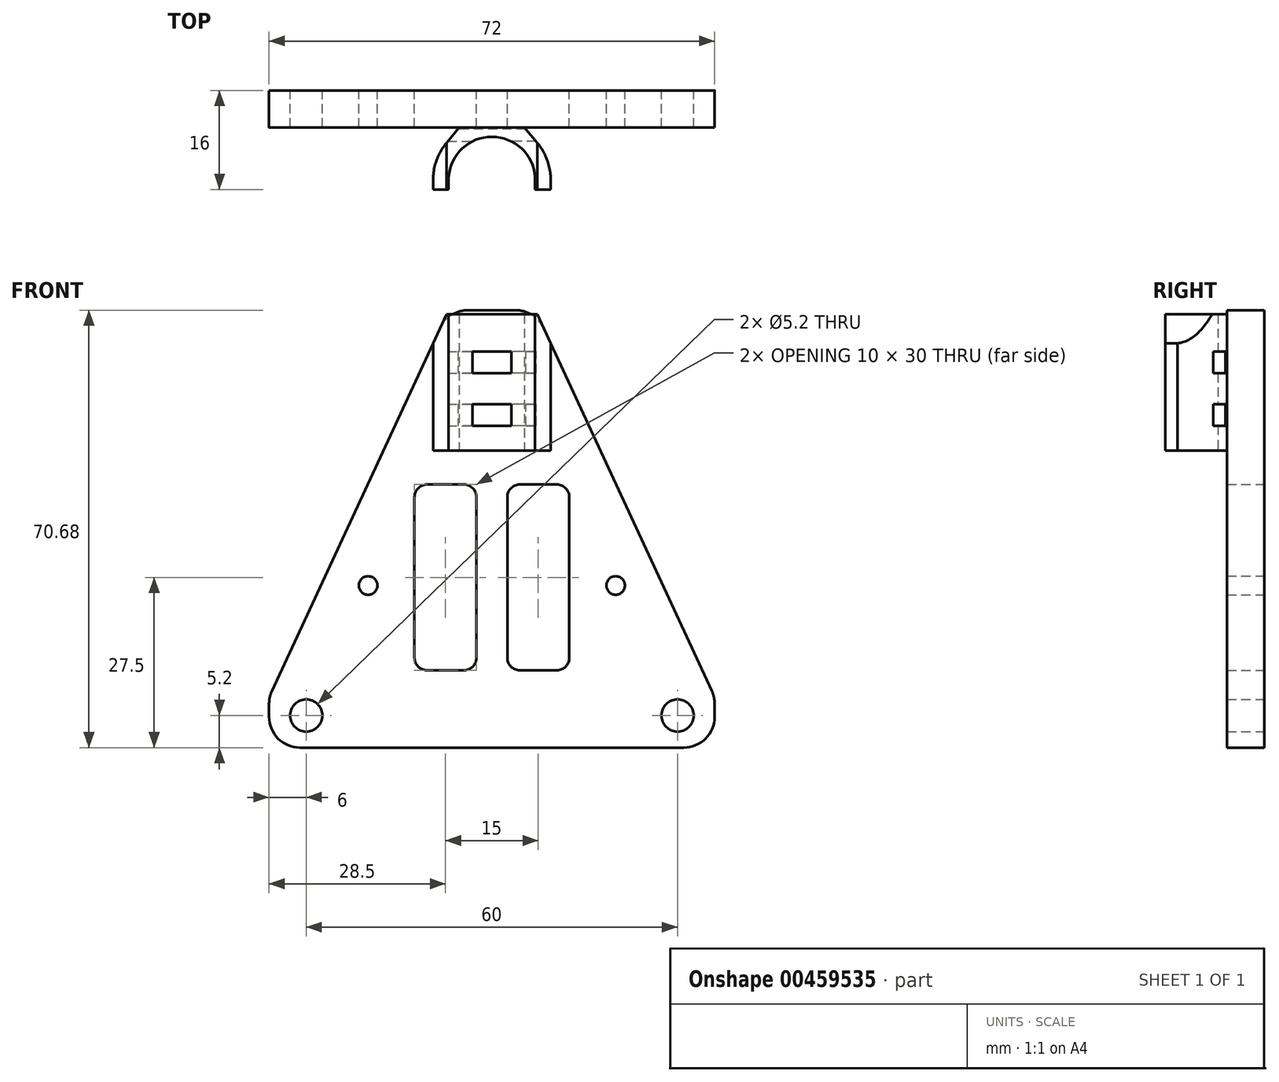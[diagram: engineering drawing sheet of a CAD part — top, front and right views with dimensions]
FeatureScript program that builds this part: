
annotation { "Feature Type Name" : "Feature", "Feature Type Description" : "" }
export const myFeature = defineFeature(function(context is Context, id is Id, definition is map)
    precondition{}
    {
        {
            var Q0;
            Q0=qCreatedBy(makeId("Front.planeOp"),FACE);
            var sketch = newSketch(context, id + "F0", { "sketchPlane" : qUnion([Q0])});
            skCircle(sketch, "E0", {"center": v(-30, 0) * mm, "radius": 2.6 * mm});
            skCircle(sketch, "E1", {"center": v(30, 0) * mm, "radius": 2.6 * mm});
            skLineSegment(sketch, "E2.bottom", {"start": v(-36, -5.2) * mm, "end": v(36, -5.2) * mm});
            skLineSegment(sketch, "E2.top", {"start": v(-36, 65.48) * mm, "end": v(36, 65.48) * mm});
            skLineSegment(sketch, "E2.left", {"start": v(-36, -5.2) * mm, "end": v(-36, 65.48) * mm});
            skLineSegment(sketch, "E2.right", {"start": v(36, -5.2) * mm, "end": v(36, 65.48) * mm});
            skLineSegment(sketch, "E3.bottom", {"start": v(-36, -5.2) * mm, "end": v(36, -5.2) * mm, "construction": true});
            skLineSegment(sketch, "E3.top", {"start": v(-36, 3) * mm, "end": v(36, 3) * mm, "construction": true});
            skLineSegment(sketch, "E3.left", {"start": v(-36, -5.2) * mm, "end": v(-36, 3) * mm, "construction": true});
            skLineSegment(sketch, "E3.right", {"start": v(36, -5.2) * mm, "end": v(36, 3) * mm, "construction": true});
            skLineSegment(sketch, "E4", {"start": v(-36, 3) * mm, "end": v(-5, 69.8) * mm});
            skLineSegment(sketch, "E5", {"start": v(36, 3) * mm, "end": v(5, 69.8) * mm});
            skLineSegment(sketch, "E6", {"start": v(5, 69.8) * mm, "end": v(-5, 69.8) * mm});
            skLineSegment(sketch, "E7.bottom", {"start": v(-12.5, 37.3) * mm, "end": v(-2.5, 37.3) * mm});
            skLineSegment(sketch, "E7.top", {"start": v(-12.5, 7.3) * mm, "end": v(-2.5, 7.3) * mm});
            skLineSegment(sketch, "E7.left", {"start": v(-12.5, 37.3) * mm, "end": v(-12.5, 7.3) * mm});
            skLineSegment(sketch, "E7.right", {"start": v(-2.5, 37.3) * mm, "end": v(-2.5, 7.3) * mm});
            skLineSegment(sketch, "E8.bottom", {"start": v(2.5, 37.3) * mm, "end": v(12.5, 37.3) * mm});
            skLineSegment(sketch, "E8.top", {"start": v(2.5, 7.3) * mm, "end": v(12.5, 7.3) * mm});
            skLineSegment(sketch, "E8.left", {"start": v(2.5, 37.3) * mm, "end": v(2.5, 7.3) * mm});
            skLineSegment(sketch, "E8.right", {"start": v(12.5, 37.3) * mm, "end": v(12.5, 7.3) * mm});
            skCircle(sketch, "E9", {"center": v(-20, 21) * mm, "radius": 1.5 * mm});
            skCircle(sketch, "E10", {"center": v(20, 21) * mm, "radius": 1.5 * mm});
            skSolve(sketch);
        }
        {
            var Q0;
            Q0=makeQuery(id+"F0.imprint","IMPRINT",FACE,{"disambiguationData":[TD([[makeQuery(id+"F0.imprint","IMPRINT",EDGE,{"derivedFrom":sQuery(id+"F0.wireOp",EDGE,"E0")}),-1.0]])]});
            extrude(context, id + "F1", {"entities" : qUnion([Q0]), "depth" : 6 * mm});
        }
        {
            var Q0;
            Q0=makeQuery(id+"F1.opExtrude","CAP_FACE",FACE,{"disambiguationData":[OSD([sQuery(id+"F0.wireOp",EDGE,"E0"),sQuery(id+"F0.wireOp",EDGE,"E1"),sQuery(id+"F0.wireOp",EDGE,"E2.bottom"),sQuery(id+"F0.wireOp",EDGE,"E2.top"),sQuery(id+"F0.wireOp",EDGE,"E2.left"),sQuery(id+"F0.wireOp",EDGE,"E2.right"),sQuery(id+"F0.wireOp",EDGE,"E4"),sQuery(id+"F0.wireOp",EDGE,"E5"),sQuery(id+"F0.wireOp",EDGE,"IImjeFes-nADZ-uSL3-nvNK-4zdbtvGVff6f"),sQuery(id+"F0.wireOp",EDGE,"sDR05uGn-SlpC-Wm0R-yilg-abFSDviSMYJG"),sQuery(id+"F0.wireOp",EDGE,"sjxaUOTC-dEMi-kEfi-0SqV-ZGTUvvVfsrZj"),sQuery(id+"F0.wireOp",EDGE,"LS0tKh8h-u9XM-H1ll-KqjH-JoQgyvfXeunZ")])],"isStart":false});
            var sketch = newSketch(context, id + "F2", { "sketchPlane" : qUnion([Q0])});
            skLineSegment(sketch, "E11.bottom", {"start": v(-10, 64.8) * mm, "end": v(10, 64.8) * mm});
            skLineSegment(sketch, "E11.top", {"start": v(-10, 42.8) * mm, "end": v(10, 42.8) * mm});
            skLineSegment(sketch, "E11.left", {"start": v(-10, 64.8) * mm, "end": v(-10, 42.8) * mm});
            skLineSegment(sketch, "E11.right", {"start": v(10, 64.8) * mm, "end": v(10, 42.8) * mm});
            skSolve(sketch);
        }
        {
            var Q0;
            {var subQ1=sQuery(id+"F2.wireOp",EDGE,"E11.top");Q0=makeQuery(id+"F2.imprint","IMPRINT",FACE,{"disambiguationData":[TD([[makeQuery(id+"F2.imprint","IMPRINT",EDGE,{"derivedFrom":subQ1}),1.0]])]});}
            extrude(context, id + "F3", {"entities" : qUnion([Q0]), "operationType" : NewBodyOperationType.ADD, "depth" : 8 * mm});
        }
        {
            var Q0;
            Q0=makeQuery(id+"F3.opExtrude","SWEPT_FACE",FACE,{"disambiguationData":[OSD([sQuery(id+"F2.wireOp",EDGE,"E11.top")])]});
            var sketch = newSketch(context, id + "F4", { "sketchPlane" : qUnion([Q0])});
            skCircle(sketch, "E12", {"center": v(0, 14.5) * mm, "radius": 7 * mm});
            skPoint(sketch, "E12.centerSnap0", {"position": v(0, 6) * mm});
            skCircle(sketch, "E13", {"center": v(0, 14.5) * mm, "radius": 9.5 * mm});
            skLineSegment(sketch, "E14", {"start": v(3.5, 3.89) * mm, "end": v(7.28, 8.4) * mm});
            skLineSegment(sketch, "E15", {"start": v(-3.5, 3.9) * mm, "end": v(-7.27, 8.4) * mm});
            skSolve(sketch);
        }
        {
            var Q0;
            {var subQ0=sQuery(id+"F4.wireOp",EDGE,"E12");var subQ1=makeQuery(id+"F3.opExtrude","CAP_EDGE",EDGE,{"disambiguationData":[OSD([sQuery(id+"F6hy1r7xXSjZawP_1.wireOp",EDGE,"ysBCCqsK-66z4-jQDk-QU8H-0Tmh3f9Fqvu1.top")])],"isStart":false});var subQ2=makeQuery(id+"F4.imprint","INTERSECT",VERTEX,{"disambiguationData":[OD(0.0)],"derivedFrom":[subQ1,subQ0]});Q0=makeQuery(id+"F4.imprint","IMPRINT",FACE,{"disambiguationData":[TD([[makeQuery(id+"F4.imprint","IMPRINT",EDGE,{"disambiguationData":[TD([[subQ2,-1.0]])],"derivedFrom":subQ0}),1.0]])]});}
            var Q1;
            {var subQ0=sQuery(id+"F4.wireOp",EDGE,"E14");Q1=makeQuery(id+"F4.imprint","IMPRINT",FACE,{"disambiguationData":[TD([[makeQuery(id+"F4.imprint","IMPRINT",EDGE,{"derivedFrom":subQ0}),-1.0]])]});}
            var Q2;
            {var subQ0=sQuery(id+"F4.wireOp",EDGE,"E15");Q2=makeQuery(id+"F4.imprint","IMPRINT",FACE,{"disambiguationData":[TD([[makeQuery(id+"F4.imprint","IMPRINT",EDGE,{"derivedFrom":subQ0}),1.0]])]});}
            extrude(context, id + "F5", {"entities" : qUnion([Q0, Q1, Q2]), "operationType" : NewBodyOperationType.REMOVE, "oppositeDirection" : true, "depth" : 25 * mm});
        }
        {
            var Q0;
            Q0=qCreatedBy(makeId("Right.planeOp"),FACE);
            var sketch = newSketch(context, id + "F6", { "sketchPlane" : qUnion([Q0])});
            skLineSegment(sketch, "E16.bottom", {"start": v(-8.25, 50.3) * mm, "end": v(-6.25, 50.3) * mm});
            skLineSegment(sketch, "E16.top", {"start": v(-8.25, 46.8) * mm, "end": v(-6.25, 46.8) * mm});
            skLineSegment(sketch, "E16.left", {"start": v(-8.25, 50.3) * mm, "end": v(-8.25, 46.8) * mm});
            skLineSegment(sketch, "E16.right", {"start": v(-6.25, 50.3) * mm, "end": v(-6.25, 46.8) * mm});
            skLineSegment(sketch, "E17.bottom", {"start": v(-8.25, 58.8) * mm, "end": v(-6.25, 58.8) * mm});
            skLineSegment(sketch, "E17.top", {"start": v(-8.25, 55.3) * mm, "end": v(-6.25, 55.3) * mm});
            skLineSegment(sketch, "E17.left", {"start": v(-8.25, 58.8) * mm, "end": v(-8.25, 55.3) * mm});
            skLineSegment(sketch, "E17.right", {"start": v(-6.25, 58.8) * mm, "end": v(-6.25, 55.3) * mm});
            skSolve(sketch);
        }
        {
            var Q0;
            Q0 = qSketchRegion(id + "F6", true);
            extrude(context, id + "F7", {"entities" : qUnion([Q0]), "operationType" : NewBodyOperationType.REMOVE, "endBound" : BoundingType.THROUGH_ALL, "depth" : 25 * mm});
        }
        {
            var Q0;
            Q0 = qSketchRegion(id + "F6", true);
            extrude(context, id + "F8", {"entities" : qUnion([Q0]), "operationType" : NewBodyOperationType.REMOVE, "oppositeDirection" : true, "depth" : 25 * mm});
        }
        {
            var Q0;
            Q0=makeQuery(id+"F1.opExtrude","SWEPT_EDGE",EDGE,{"disambiguationData":[OSD([sQuery(id+"F0.wireOp",EDGE,"E2.bottom"),sQuery(id+"F0.wireOp",EDGE,"E2.left")])]});
            var Q1;
            Q1=makeQuery(id+"F1.opExtrude","SWEPT_EDGE",EDGE,{"disambiguationData":[OSD([sQuery(id+"F0.wireOp",EDGE,"E2.bottom"),sQuery(id+"F0.wireOp",EDGE,"E2.right")])]});
            var Q2;
            Q2=makeQuery(id+"F1.opExtrude","SWEPT_EDGE",EDGE,{"disambiguationData":[OSD([sQuery(id+"F0.wireOp",EDGE,"E5"),sQuery(id+"F0.wireOp",EDGE,"E6")])]});
            var Q3;
            Q3=makeQuery(id+"F1.opExtrude","SWEPT_EDGE",EDGE,{"disambiguationData":[OSD([sQuery(id+"F0.wireOp",EDGE,"E4"),sQuery(id+"F0.wireOp",EDGE,"E6")])]});
            var Q4;
            Q4=makeQuery(id+"F1.opExtrude","SWEPT_EDGE",EDGE,{"disambiguationData":[OSD([sQuery(id+"F0.wireOp",EDGE,"E2.right"),sQuery(id+"F0.wireOp",EDGE,"E5")])]});
            var Q5;
            Q5=makeQuery(id+"F1.opExtrude","SWEPT_EDGE",EDGE,{"disambiguationData":[OSD([sQuery(id+"F0.wireOp",EDGE,"E2.left"),sQuery(id+"F0.wireOp",EDGE,"E4")])]});
            var Q6;
            Q6=makeQuery(id+"F1.opExtrude","SWEPT_EDGE",EDGE,{"disambiguationData":[OSD([sQuery(id+"F0.wireOp",EDGE,"IImjeFes-nADZ-uSL3-nvNK-4zdbtvGVff6f"),sQuery(id+"F0.wireOp",EDGE,"sDR05uGn-SlpC-Wm0R-yilg-abFSDviSMYJG")])]});
            var Q7;
            Q7=makeQuery(id+"F1.opExtrude","SWEPT_EDGE",EDGE,{"disambiguationData":[OSD([sQuery(id+"F0.wireOp",EDGE,"IImjeFes-nADZ-uSL3-nvNK-4zdbtvGVff6f"),sQuery(id+"F0.wireOp",EDGE,"LS0tKh8h-u9XM-H1ll-KqjH-JoQgyvfXeunZ")])]});
            var Q8;
            Q8=makeQuery(id+"F1.opExtrude","SWEPT_EDGE",EDGE,{"disambiguationData":[OSD([sQuery(id+"F0.wireOp",EDGE,"sjxaUOTC-dEMi-kEfi-0SqV-ZGTUvvVfsrZj"),sQuery(id+"F0.wireOp",EDGE,"LS0tKh8h-u9XM-H1ll-KqjH-JoQgyvfXeunZ")])]});
            var Q9;
            Q9=makeQuery(id+"F1.opExtrude","SWEPT_EDGE",EDGE,{"disambiguationData":[OSD([sQuery(id+"F0.wireOp",EDGE,"sDR05uGn-SlpC-Wm0R-yilg-abFSDviSMYJG"),sQuery(id+"F0.wireOp",EDGE,"sjxaUOTC-dEMi-kEfi-0SqV-ZGTUvvVfsrZj")])]});
            fillet(context, id + "F9", {"entities" : qUnion([Q0, Q1, Q2, Q3, Q4, Q5, Q6, Q7, Q8, Q9]), "radius" : 5 * mm, "tangentPropagation" : true, "allowEdgeOverflow" : false});
        }
        {
            var Q0;
            {var subQ0=sQuery(id+"F4.wireOp",EDGE,"E13");Q0=makeQuery(id+"F7.boolean.opBoolean","INTERSECT",EDGE,{"derivedFrom":[makeQuery(id+"F5.boolean.opBoolean","COPY",FACE,{"derivedFrom":makeQuery(id+"F5.opExtrude","SWEPT_FACE",FACE,{"disambiguationData":[OSD([subQ0]),TDD([makeQuery(id+"F4.imprint","IMPRINT",EDGE,{"disambiguationData":[TD([[makeQuery(id+"F4.imprint","INTERSECT",VERTEX,{"derivedFrom":[subQ0,sQuery(id+"F4.wireOp",EDGE,"E14")]}),-1.0]])],"derivedFrom":subQ0})])]})}),makeQuery(id+"F7.opExtrude","SWEPT_FACE",FACE,{"disambiguationData":[OSD([sQuery(id+"F6.wireOp",EDGE,"E16.left")])]})]});}
            var Q1;
            {var subQ0=sQuery(id+"F4.wireOp",EDGE,"E13");Q1=makeQuery(id+"F7.boolean.opBoolean","INTERSECT",EDGE,{"derivedFrom":[makeQuery(id+"F5.boolean.opBoolean","COPY",FACE,{"derivedFrom":makeQuery(id+"F5.opExtrude","SWEPT_FACE",FACE,{"disambiguationData":[OSD([subQ0]),TDD([makeQuery(id+"F4.imprint","IMPRINT",EDGE,{"disambiguationData":[TD([[makeQuery(id+"F4.imprint","INTERSECT",VERTEX,{"derivedFrom":[subQ0,sQuery(id+"F4.wireOp",EDGE,"E14")]}),-1.0]])],"derivedFrom":subQ0})])]})}),makeQuery(id+"F7.opExtrude","SWEPT_FACE",FACE,{"disambiguationData":[OSD([sQuery(id+"F6.wireOp",EDGE,"E17.left")])]})]});}
            var Q2;
            {var subQ0=sQuery(id+"F4.wireOp",EDGE,"E13");Q2=makeQuery(id+"F8.boolean.opBoolean","INTERSECT",EDGE,{"derivedFrom":[makeQuery(id+"F5.boolean.opBoolean","COPY",FACE,{"derivedFrom":makeQuery(id+"F5.opExtrude","SWEPT_FACE",FACE,{"disambiguationData":[OSD([subQ0]),TDD([makeQuery(id+"F4.imprint","IMPRINT",EDGE,{"disambiguationData":[TD([[makeQuery(id+"F4.imprint","INTERSECT",VERTEX,{"derivedFrom":[subQ0,sQuery(id+"F4.wireOp",EDGE,"E15")]}),1.0]])],"derivedFrom":subQ0})])]})}),makeQuery(id+"F8.opExtrude","SWEPT_FACE",FACE,{"disambiguationData":[OSD([sQuery(id+"F6.wireOp",EDGE,"E17.left")])]})]});}
            var Q3;
            {var subQ0=sQuery(id+"F4.wireOp",EDGE,"E13");Q3=makeQuery(id+"F8.boolean.opBoolean","INTERSECT",EDGE,{"derivedFrom":[makeQuery(id+"F5.boolean.opBoolean","COPY",FACE,{"derivedFrom":makeQuery(id+"F5.opExtrude","SWEPT_FACE",FACE,{"disambiguationData":[OSD([subQ0]),TDD([makeQuery(id+"F4.imprint","IMPRINT",EDGE,{"disambiguationData":[TD([[makeQuery(id+"F4.imprint","INTERSECT",VERTEX,{"derivedFrom":[subQ0,sQuery(id+"F4.wireOp",EDGE,"E15")]}),1.0]])],"derivedFrom":subQ0})])]})}),makeQuery(id+"F8.opExtrude","SWEPT_FACE",FACE,{"disambiguationData":[OSD([sQuery(id+"F6.wireOp",EDGE,"E16.left")])]})]});}
            var Q4;
            Q4=makeQuery(id+"F1.opExtrude","SWEPT_EDGE",EDGE,{"disambiguationData":[OSD([sQuery(id+"F0.wireOp",EDGE,"E7.bottom"),sQuery(id+"F0.wireOp",EDGE,"E7.left")])]});
            var Q5;
            Q5=makeQuery(id+"F1.opExtrude","SWEPT_EDGE",EDGE,{"disambiguationData":[OSD([sQuery(id+"F0.wireOp",EDGE,"E7.top"),sQuery(id+"F0.wireOp",EDGE,"E7.left")])]});
            var Q6;
            Q6=makeQuery(id+"F1.opExtrude","SWEPT_EDGE",EDGE,{"disambiguationData":[OSD([sQuery(id+"F0.wireOp",EDGE,"E7.top"),sQuery(id+"F0.wireOp",EDGE,"E7.right")])]});
            var Q7;
            Q7=makeQuery(id+"F1.opExtrude","SWEPT_EDGE",EDGE,{"disambiguationData":[OSD([sQuery(id+"F0.wireOp",EDGE,"E8.top"),sQuery(id+"F0.wireOp",EDGE,"E8.right")])]});
            var Q8;
            Q8=makeQuery(id+"F1.opExtrude","SWEPT_EDGE",EDGE,{"disambiguationData":[OSD([sQuery(id+"F0.wireOp",EDGE,"E8.bottom"),sQuery(id+"F0.wireOp",EDGE,"E8.right")])]});
            var Q9;
            Q9=makeQuery(id+"F1.opExtrude","SWEPT_EDGE",EDGE,{"disambiguationData":[OSD([sQuery(id+"F0.wireOp",EDGE,"E7.bottom"),sQuery(id+"F0.wireOp",EDGE,"E7.right")])]});
            var Q10;
            Q10=makeQuery(id+"F1.opExtrude","SWEPT_EDGE",EDGE,{"disambiguationData":[OSD([sQuery(id+"F0.wireOp",EDGE,"E8.bottom"),sQuery(id+"F0.wireOp",EDGE,"E8.left")])]});
            var Q11;
            Q11=makeQuery(id+"F1.opExtrude","SWEPT_EDGE",EDGE,{"disambiguationData":[OSD([sQuery(id+"F0.wireOp",EDGE,"E8.top"),sQuery(id+"F0.wireOp",EDGE,"E8.left")])]});
            fillet(context, id + "F10", {"entities" : qUnion([Q0, Q1, Q2, Q3, Q4, Q5, Q6, Q7, Q8, Q9, Q10, Q11]), "radius" : 2 * mm, "tangentPropagation" : true, "allowEdgeOverflow" : false});
        }
        {
            var Q0;
            {var subQ0=sQuery(id+"F0.wireOp",EDGE,"E4");var subQ1=sQuery(id+"F2.wireOp",EDGE,"E11.top");Q0=makeQuery(id+"F5.boolean.opBoolean","SPLIT",FACE,{"disambiguationData":[TD([makeQuery(id+"F1.opExtrude","SWEPT_FACE",FACE,{"disambiguationData":[OSD([subQ0])]})])],"derivedFrom":makeQuery(id+"F3.opExtrude","CAP_FACE",FACE,{"disambiguationData":[OSD([subQ0,sQuery(id+"F0.wireOp",EDGE,"E5"),sQuery(id+"F2.wireOp",EDGE,"E11.bottom"),subQ1,sQuery(id+"F2.wireOp",EDGE,"E11.left"),sQuery(id+"F2.wireOp",EDGE,"E11.right")])],"isStart":false})});}
            var Q1;
            {var subQ0=sQuery(id+"F0.wireOp",EDGE,"E5");var subQ1=sQuery(id+"F2.wireOp",EDGE,"E11.top");Q1=makeQuery(id+"F5.boolean.opBoolean","SPLIT",FACE,{"disambiguationData":[TD([makeQuery(id+"F1.opExtrude","SWEPT_FACE",FACE,{"disambiguationData":[OSD([subQ0])]})])],"derivedFrom":makeQuery(id+"F3.opExtrude","CAP_FACE",FACE,{"disambiguationData":[OSD([sQuery(id+"F0.wireOp",EDGE,"E4"),subQ0,sQuery(id+"F2.wireOp",EDGE,"E11.bottom"),subQ1,sQuery(id+"F2.wireOp",EDGE,"E11.left"),sQuery(id+"F2.wireOp",EDGE,"E11.right")])],"isStart":false})});}
            extrude(context, id + "F11", {"entities" : qUnion([Q0, Q1]), "operationType" : NewBodyOperationType.ADD, "depth" : 2 * mm});
        }
    });
